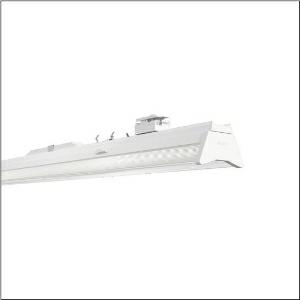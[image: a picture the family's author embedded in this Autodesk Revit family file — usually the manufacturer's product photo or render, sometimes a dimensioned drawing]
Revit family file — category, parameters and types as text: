
# Revit family: licross_r__11_performance_mo_51td167n485g_c044
name_source: partatom
category: Lighting Fixtures
units: mm (PartAtom-declared; Revit-internal decimal feet)

## family parameters
Cut with Voids When Loaded = No
Host = Face
Light Source = No
Part Type = Normal
Room Calculation Point = No
Round Connector Dimension = Use Diameter
Shared = No

## types (1)
- Licross® 11 Performance MO (1 x LED, 8840 lm, 48.6 W, 4000K)
    Apparent Load = 49 VA
    CIE Flux Codes = 66 88 96 79 100
    Color Rendering = 80
    Color Temperature = 4000K
    Default Elevation = 1800 mm
    Description = Licross® 11 Performance MO, luminaire insert, of sheet steel, galvanised, coil coated, white, length: 1.500mm, width: 120mm, height: 123mm, LED rated luminous flux: 8.840lm, light colour: 840, control gear: ON/OFF, with plug, 3-pole, with phase selection, mains connection: 220..240V, AC, 50/60Hz, rated input power: 49W, halogen-free wiring, primary light control with lens, of plastic, primary optical cover: cover, of PMMA, light emission: direct/indirect distribution, primary light characteristic: symmetric, protection rating (complete): IP54, insulation class (complete): insulation class I (protective earthing), certification: CE, ENEC, VDE, UKCA, protection symbol: D if used in an environment with non-conductive dust loads with corresponding accessories, impact resistance: IK06, permissible ambient temperature for indoor applications: -25..+35°C, corresponds to IFS (International Featured Standards) requirements for safety and quality in the food industry, reducing of maximum allowable ambient temperature of 5°C with ceiling mounting, LABS conformity tested according to VDMA 24364:2018-05, packaging unit: 1 piece
    Height = 114 mm
    Lamp = 1 x LED
    Lamp Light Flux = 8840 lm
    Lamp Power = 48.6 W
    Lamp count = 1
    Length = 1500 mm
    Luminous efficacy = 182 lm/W
    Manufacturer = Siteco
    ModVariant = No
    Model = 51TD167N485G
    Mounting Place = Ceiling
    Mounting Type = Pendant
    Number of Poles = 1
    OnlyDefault = Yes
    Power Factor = 1
    Product Name = Licross® 11 Performance MO
    Product group = luminaire insert
    ProductGroupID = 902
    Protection Class = Protection class I
    Protection Degree = IP 54
    RLX_Detail_Level = 1
    RLX_Emergency_Light_Flux = 0 lm
    RLX_Emergency_Type = 0
    RLX_Emergency_Type_DB = No
    RlxData = <blob elided: 30385 chars, md5=aa9df6fc>
    Socket = socket
    Standby Power = 0 W
    System Light Flux = 8840 lm
    System Power = 49 W
    Type Comments = Product without accessories
    Type Image = l_1256138.jpg
    URL = http://relux.com
    VarID = ---
    Voltage = 0 V
    Weight = 0.00 kg
    Width = 120 mm

## geometry (parser evidence)
native form markers: Blend x4, Sweep x13
no freeform markers — native parametric forms only
